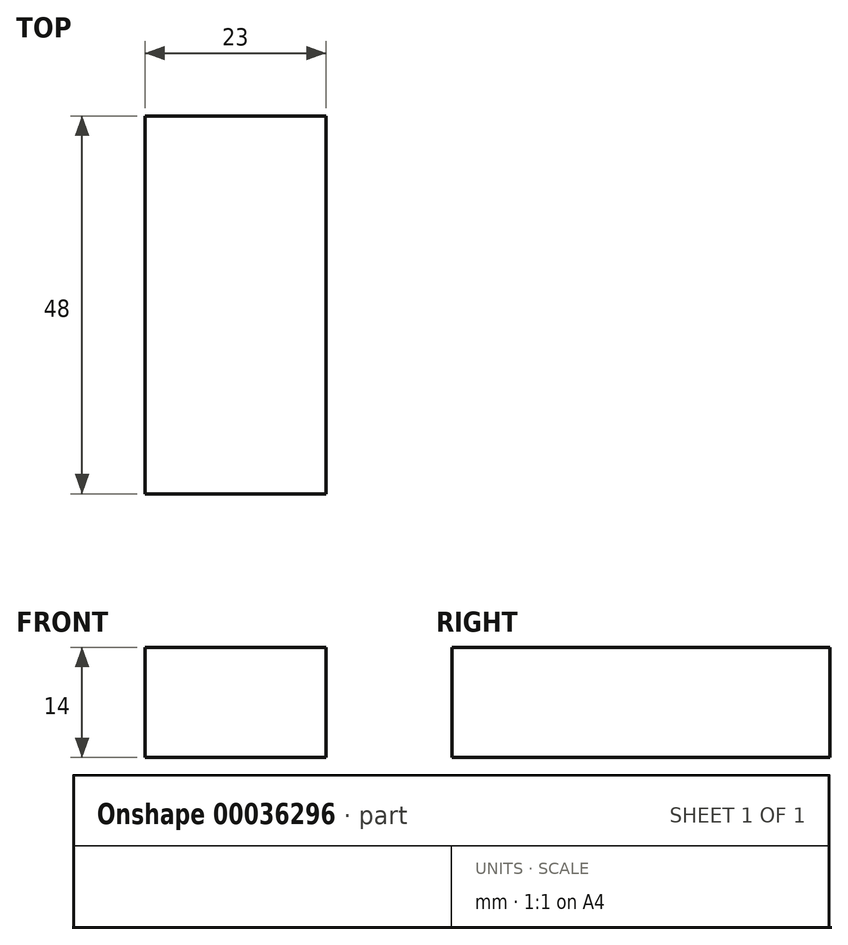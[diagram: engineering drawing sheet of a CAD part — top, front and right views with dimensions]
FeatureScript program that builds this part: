
annotation { "Feature Type Name" : "Feature", "Feature Type Description" : "" }
export const myFeature = defineFeature(function(context is Context, id is Id, definition is map)
    precondition{}
    {
        {
            var Q0;
            Q0=qCreatedBy(makeId("Top.planeOp"),FACE);
            var sketch = newSketch(context, id + "F0", { "sketchPlane" : qUnion([Q0])});
            skLineSegment(sketch, "E0.bottom", {"start": v(0, 0) * mm, "end": v(23, 0) * mm});
            skLineSegment(sketch, "E0.top", {"start": v(0, -48) * mm, "end": v(23, -48) * mm});
            skLineSegment(sketch, "E0.left", {"start": v(0, 0) * mm, "end": v(0, -48) * mm});
            skLineSegment(sketch, "E0.right", {"start": v(23, 0) * mm, "end": v(23, -48) * mm});
            skSolve(sketch);
        }
        {
            var Q0;
            Q0=makeQuery(id+"F0.imprint","IMPRINT",FACE,{"disambiguationData":[TD([[makeQuery(id+"F0.imprint","IMPRINT",EDGE,{"derivedFrom":sQuery(id+"F0.wireOp",EDGE,"E0.bottom")}),-1.0]])]});
            extrude(context, id + "F1", {"entities" : qUnion([Q0]), "depth" : 14 * mm});
        }
    });
